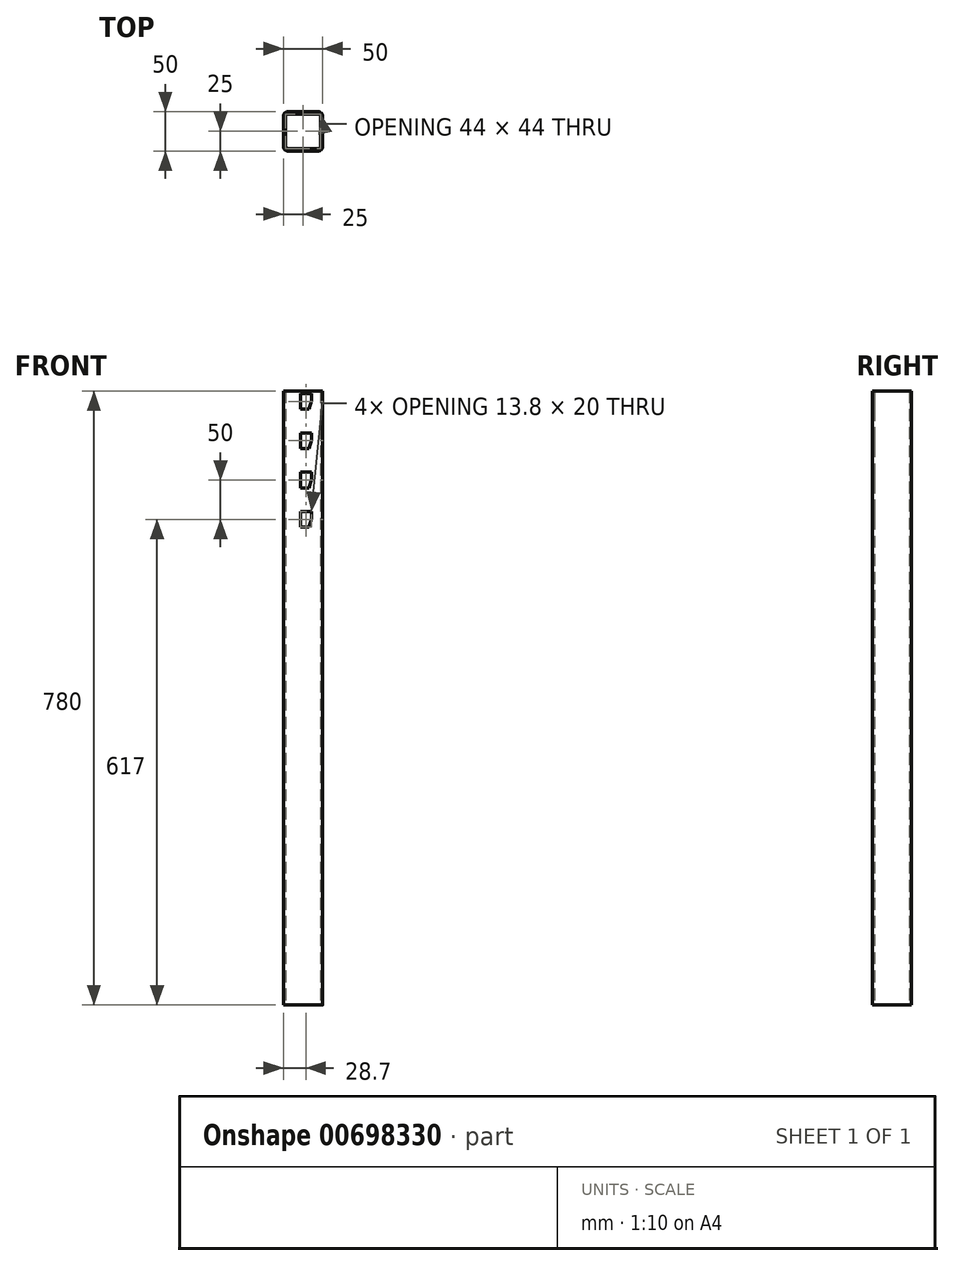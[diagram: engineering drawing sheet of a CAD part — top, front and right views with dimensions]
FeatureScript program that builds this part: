
annotation { "Feature Type Name" : "Feature", "Feature Type Description" : "" }
export const myFeature = defineFeature(function(context is Context, id is Id, definition is map)
    precondition{}
    {
        {
            var Q0;
            Q0=qCreatedBy(makeId("Top.planeOp"),FACE);
            var sketch = newSketch(context, id + "F0", { "sketchPlane" : qUnion([Q0])});
            skLineSegment(sketch, "E0.bottom", {"start": v(19, -25) * mm, "end": v(-19, -25) * mm});
            skLineSegment(sketch, "E0.top", {"start": v(19, 25) * mm, "end": v(-19, 25) * mm});
            skLineSegment(sketch, "E0.left", {"start": v(25, -19) * mm, "end": v(25, 19) * mm});
            skLineSegment(sketch, "E0.right", {"start": v(-25, -19) * mm, "end": v(-25, 19) * mm});
            skPoint(sketch, "E0.middle", {"position": v(0, 0) * mm});
            skLineSegment(sketch, "E1.bottom", {"start": v(19, 22) * mm, "end": v(-19, 22) * mm});
            skLineSegment(sketch, "E1.top", {"start": v(19, -22) * mm, "end": v(-19, -22) * mm});
            skLineSegment(sketch, "E1.left", {"start": v(22, 19) * mm, "end": v(22, -19) * mm});
            skLineSegment(sketch, "E1.right", {"start": v(-22, 19) * mm, "end": v(-22, -19) * mm});
            skPoint(sketch, "E2.visualSharp", {"position": v(-25, -25) * mm});
            skArc(sketch, "E2.filletArc", {"start": v(-25, -19) * mm, "mid": v(-23.24, -23.24) * mm, "end": v(-19, -25) * mm});
            skPoint(sketch, "E3.visualSharp", {"position": v(25, -25) * mm});
            skArc(sketch, "E3.filletArc", {"start": v(19, -25) * mm, "mid": v(23.24, -23.24) * mm, "end": v(25, -19) * mm});
            skPoint(sketch, "E4.visualSharp", {"position": v(25, 25) * mm});
            skArc(sketch, "E4.filletArc", {"start": v(25, 19) * mm, "mid": v(23.24, 23.24) * mm, "end": v(19, 25) * mm});
            skPoint(sketch, "E5.visualSharp", {"position": v(-25, 25) * mm});
            skArc(sketch, "E5.filletArc", {"start": v(-19, 25) * mm, "mid": v(-23.24, 23.24) * mm, "end": v(-25, 19) * mm});
            skPoint(sketch, "E6.visualSharp", {"position": v(-22, 22) * mm});
            skArc(sketch, "E6.filletArc", {"start": v(-19, 22) * mm, "mid": v(-21.12, 21.12) * mm, "end": v(-22, 19) * mm});
            skPoint(sketch, "E7.visualSharp", {"position": v(22, 22) * mm});
            skArc(sketch, "E7.filletArc", {"start": v(22, 19) * mm, "mid": v(21.12, 21.12) * mm, "end": v(19, 22) * mm});
            skPoint(sketch, "E8.visualSharp", {"position": v(22, -22) * mm});
            skArc(sketch, "E8.filletArc", {"start": v(19, -22) * mm, "mid": v(21.12, -21.12) * mm, "end": v(22, -19) * mm});
            skPoint(sketch, "E9.visualSharp", {"position": v(-22, -22) * mm});
            skArc(sketch, "E9.filletArc", {"start": v(-22, -19) * mm, "mid": v(-21.12, -21.12) * mm, "end": v(-19, -22) * mm});
            skSolve(sketch);
        }
        {
            var Q0;
            Q0=makeQuery(id+"F0.imprint","IMPRINT",FACE,{"disambiguationData":[TD([[makeQuery(id+"F0.imprint","IMPRINT",EDGE,{"derivedFrom":sQuery(id+"F0.wireOp",EDGE,"E0.bottom")}),-1.0]])]});
            extrude(context, id + "F1", {"entities" : qUnion([Q0]), "depth" : 780 * mm, "offsetDistance" : 25 * mm});
        }
        {
            var Q0;
            Q0=makeQuery(id+"F1.opExtrude","SWEPT_FACE",FACE,{"disambiguationData":[OSD([sQuery(id+"F0.wireOp",EDGE,"E0.bottom")])]});
            var sketch = newSketch(context, id + "F2", { "sketchPlane" : qUnion([Q0])});
            skLineSegment(sketch, "E10", {"start": v(-3.2, 777) * mm, "end": v(10.6, 777) * mm});
            skLineSegment(sketch, "E11", {"start": v(10.6, 777) * mm, "end": v(10.6, 768) * mm});
            skLineSegment(sketch, "E12", {"start": v(10.6, 768) * mm, "end": v(7.6, 757) * mm});
            skLineSegment(sketch, "E13", {"start": v(7.6, 757) * mm, "end": v(-3.2, 757) * mm});
            skLineSegment(sketch, "E14", {"start": v(-3.2, 757) * mm, "end": v(-3.2, 777) * mm});
            skLineSegment(sketch, "E15.0.1.0", {"start": v(-3.2, 707) * mm, "end": v(-3.2, 727) * mm});
            skLineSegment(sketch, "E15.0.1.1", {"start": v(-3.2, 727) * mm, "end": v(10.6, 727) * mm});
            skLineSegment(sketch, "E15.0.1.2", {"start": v(10.6, 727) * mm, "end": v(10.6, 718) * mm});
            skLineSegment(sketch, "E15.0.1.3", {"start": v(10.6, 718) * mm, "end": v(7.6, 707) * mm});
            skLineSegment(sketch, "E15.0.1.4", {"start": v(7.6, 707) * mm, "end": v(-3.2, 707) * mm});
            skLineSegment(sketch, "E15.0.2.0", {"start": v(-3.2, 657) * mm, "end": v(-3.2, 677) * mm});
            skLineSegment(sketch, "E15.0.2.1", {"start": v(-3.2, 677) * mm, "end": v(10.6, 677) * mm});
            skLineSegment(sketch, "E15.0.2.2", {"start": v(10.6, 677) * mm, "end": v(10.6, 668) * mm});
            skLineSegment(sketch, "E15.0.2.3", {"start": v(10.6, 668) * mm, "end": v(7.6, 657) * mm});
            skLineSegment(sketch, "E15.0.2.4", {"start": v(7.6, 657) * mm, "end": v(-3.2, 657) * mm});
            skLineSegment(sketch, "E15.0.3.0", {"start": v(-3.2, 607) * mm, "end": v(-3.2, 627) * mm});
            skLineSegment(sketch, "E15.0.3.1", {"start": v(-3.2, 627) * mm, "end": v(10.6, 627) * mm});
            skLineSegment(sketch, "E15.0.3.2", {"start": v(10.6, 627) * mm, "end": v(10.6, 618) * mm});
            skLineSegment(sketch, "E15.0.3.3", {"start": v(10.6, 618) * mm, "end": v(7.6, 607) * mm});
            skLineSegment(sketch, "E15.0.3.4", {"start": v(7.6, 607) * mm, "end": v(-3.2, 607) * mm});
            skLineSegment(sketch, "E15.direction1", {"start": v(-3.2, 757) * mm, "end": v(21.8, 757) * mm, "construction": true});
            skLineSegment(sketch, "E15.direction2", {"start": v(-3.2, 757) * mm, "end": v(-3.2, 707) * mm, "construction": true});
            skSolve(sketch);
        }
        {
            var Q0;
            Q0=makeQuery(id+"F2.imprint","IMPRINT",FACE,{"disambiguationData":[TD([[makeQuery(id+"F2.imprint","IMPRINT",EDGE,{"derivedFrom":sQuery(id+"F2.wireOp",EDGE,"E10")}),-1.0]])]});
            var Q1;
            Q1=makeQuery(id+"F2.imprint","IMPRINT",FACE,{"disambiguationData":[TD([[makeQuery(id+"F2.imprint","IMPRINT",EDGE,{"derivedFrom":sQuery(id+"F2.wireOp",EDGE,"E15.0.1.0")}),-1.0]])]});
            var Q2;
            Q2=makeQuery(id+"F2.imprint","IMPRINT",FACE,{"disambiguationData":[TD([[makeQuery(id+"F2.imprint","IMPRINT",EDGE,{"derivedFrom":sQuery(id+"F2.wireOp",EDGE,"E15.0.2.0")}),-1.0]])]});
            var Q3;
            Q3=makeQuery(id+"F2.imprint","IMPRINT",FACE,{"disambiguationData":[TD([[makeQuery(id+"F2.imprint","IMPRINT",EDGE,{"derivedFrom":sQuery(id+"F2.wireOp",EDGE,"E15.0.3.0")}),-1.0]])]});
            extrude(context, id + "F3", {"entities" : qUnion([Q0, Q1, Q2, Q3]), "operationType" : NewBodyOperationType.REMOVE, "oppositeDirection" : true, "depth" : 3 * mm, "offsetDistance" : 25 * mm});
        }
    });
